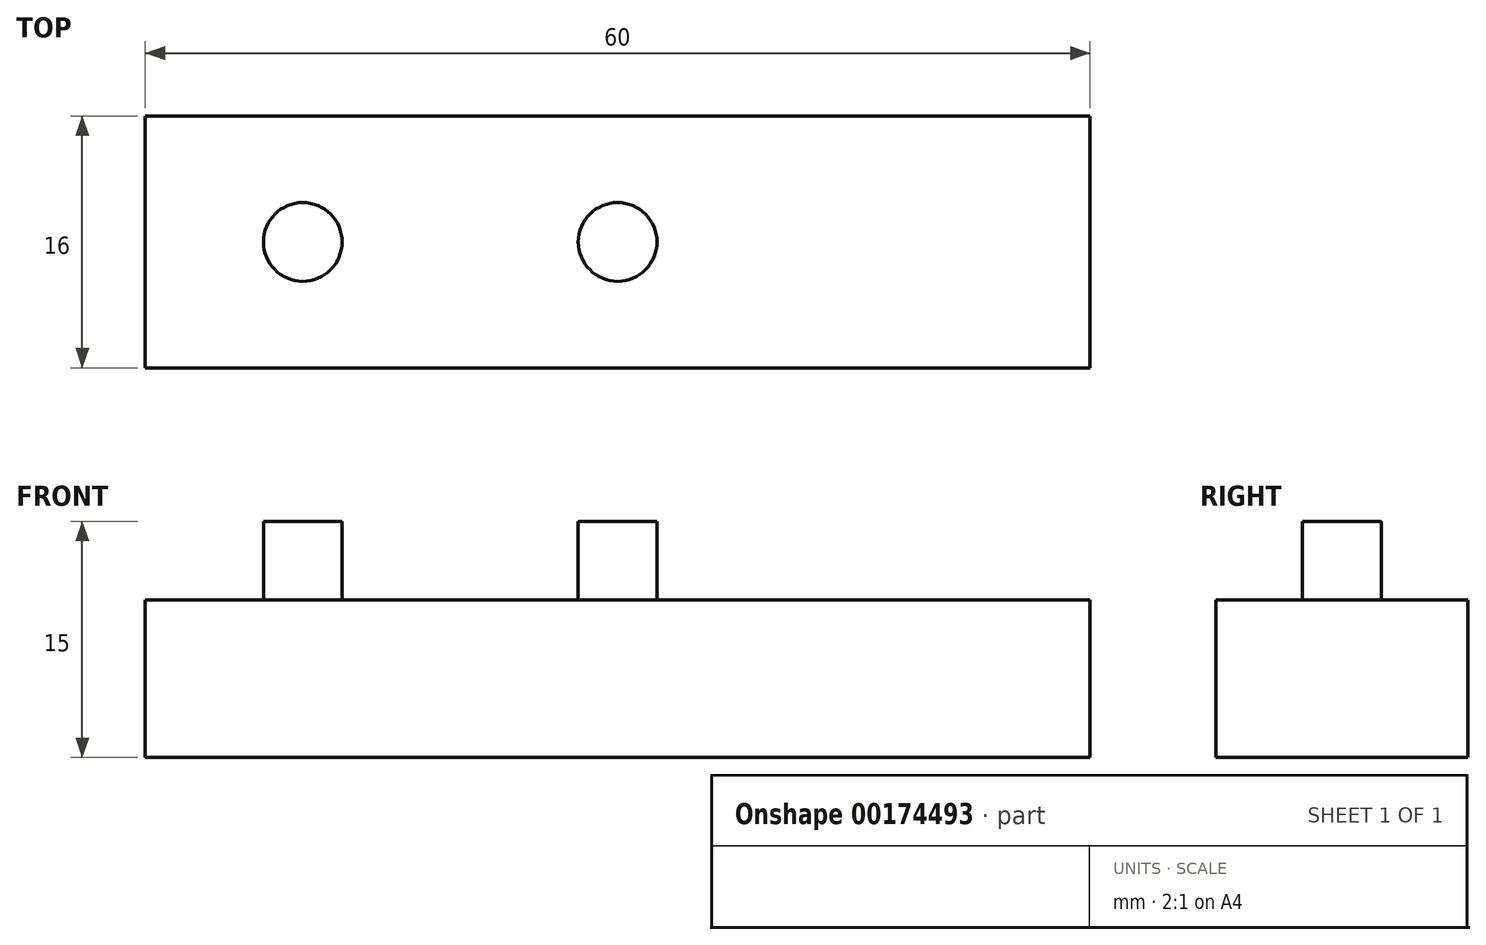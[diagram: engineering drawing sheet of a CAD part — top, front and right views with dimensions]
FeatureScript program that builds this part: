
annotation { "Feature Type Name" : "Feature", "Feature Type Description" : "" }
export const myFeature = defineFeature(function(context is Context, id is Id, definition is map)
    precondition{}
    {
        {
            var Q0;
            Q0=qCreatedBy(makeId("Top.planeOp"),FACE);
            var sketch = newSketch(context, id + "F0", { "sketchPlane" : qUnion([Q0])});
            skLineSegment(sketch, "E0.bottom", {"start": v(-30, 8) * mm, "end": v(30, 8) * mm});
            skLineSegment(sketch, "E0.top", {"start": v(-30, -8) * mm, "end": v(30, -8) * mm});
            skLineSegment(sketch, "E0.left", {"start": v(-30, 8) * mm, "end": v(-30, -8) * mm});
            skLineSegment(sketch, "E0.right", {"start": v(30, 8) * mm, "end": v(30, -8) * mm});
            skSolve(sketch);
        }
        {
            var Q0;
            Q0=makeQuery(id+"F0.imprint","IMPRINT",FACE,{"disambiguationData":[TD([[makeQuery(id+"F0.imprint","IMPRINT",EDGE,{"derivedFrom":sQuery(id+"F0.wireOp",EDGE,"E0.bottom")}),-1.0]])]});
            extrude(context, id + "F1", {"entities" : qUnion([Q0]), "depth" : 10 * mm});
        }
        {
            var Q0;
            Q0=makeQuery(id+"F1.opExtrude","CAP_FACE",FACE,{"disambiguationData":[OSD([sQuery(id+"F0.wireOp",EDGE,"E0.bottom"),sQuery(id+"F0.wireOp",EDGE,"E0.top"),sQuery(id+"F0.wireOp",EDGE,"E0.left"),sQuery(id+"F0.wireOp",EDGE,"E0.right")])],"isStart":false});
            var sketch = newSketch(context, id + "F2", { "sketchPlane" : qUnion([Q0])});
            skCircle(sketch, "E1", {"center": v(-20, 0) * mm, "radius": 2.5 * mm});
            skCircle(sketch, "E2", {"center": v(0, 0) * mm, "radius": 2.5 * mm});
            skSolve(sketch);
        }
        {
            var Q0;
            Q0=makeQuery(id+"F2.imprint","IMPRINT",FACE,{"disambiguationData":[TD([[makeQuery(id+"F2.imprint","IMPRINT",EDGE,{"derivedFrom":sQuery(id+"F2.wireOp",EDGE,"E2")}),1.0]])]});
            extrude(context, id + "F3", {"entities" : qUnion([Q0]), "operationType" : NewBodyOperationType.ADD, "depth" : 5 * mm});
        }
        {
            var Q0;
            Q0 = qSketchRegion(id + "F2", true);
            extrude(context, id + "F4", {"entities" : qUnion([Q0]), "operationType" : NewBodyOperationType.ADD, "depth" : 5 * mm});
        }
    });
